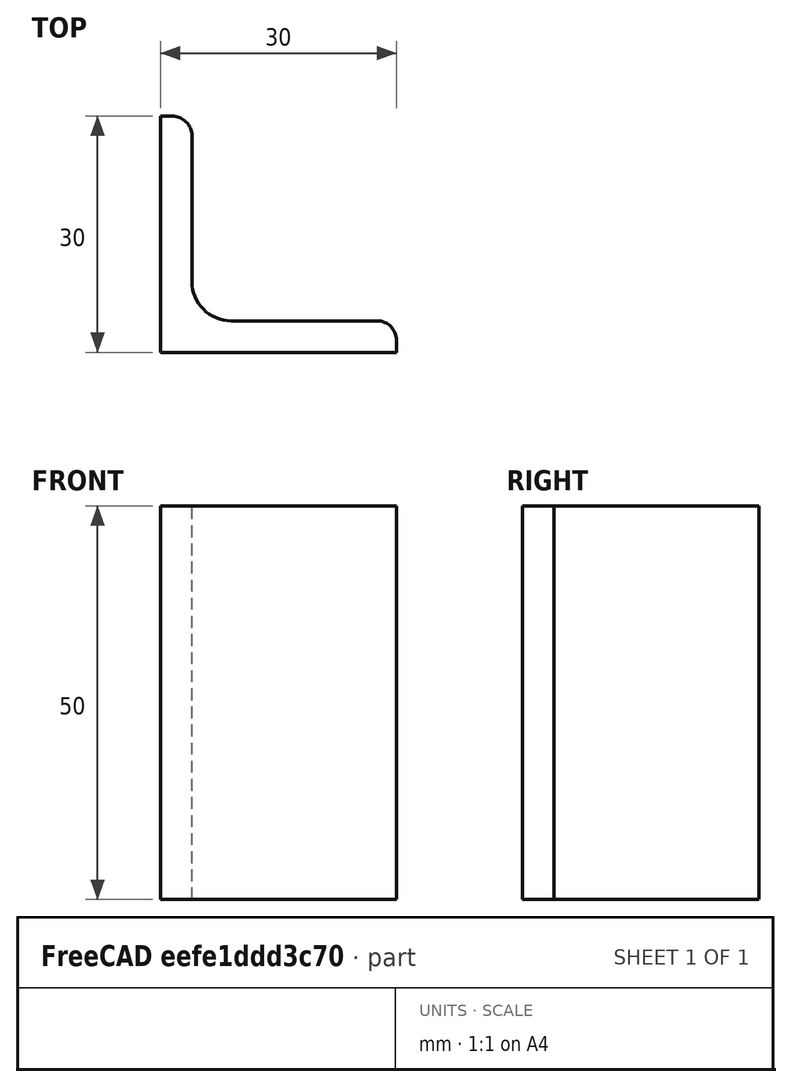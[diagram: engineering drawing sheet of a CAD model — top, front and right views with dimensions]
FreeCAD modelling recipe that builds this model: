
FCSTD DOCUMENT  (FreeCAD 0.15R4671 (Git))
Label: Angle Bar L30x30x4 EN10056 S235JR
License: All rights reserved
LicenseURL: http://en.wikipedia.org/wiki/All_rights_reserved
objects: Sketcher::SketchObject×1, Part::Extrusion×1
note: 2 computed .brp shape members not serialized (recipe doc carries the construction recipe); baked Part::Feature solids carry a one-line shape summary decoded from their .brp

FEATURE [Sketcher::SketchObject] Sketch
  sketch-geometry (9):
    g0: LineSegment StartX=0 StartY=0 StartZ=0 EndX=30 EndY=0 EndZ=0
    g1: LineSegment StartX=30 StartY=0 StartZ=0 EndX=30 EndY=1.5 EndZ=0
    g2: LineSegment StartX=27.5 StartY=4 StartZ=0 EndX=9 EndY=4 EndZ=0
    g3: LineSegment StartX=0 StartY=0 StartZ=0 EndX=0 EndY=30 EndZ=0
    g4: LineSegment StartX=0 StartY=30 StartZ=0 EndX=1.5 EndY=30 EndZ=0
    g5: LineSegment StartX=4 StartY=27.5 StartZ=0 EndX=4 EndY=9 EndZ=0
    g6: ArcOfCircle CenterX=9 CenterY=9 CenterZ=0 NormalX=0 NormalY=0 NormalZ=1 Radius=5 StartAngle=3.14159 EndAngle=4.71239
    g7: ArcOfCircle CenterX=1.5 CenterY=27.5 CenterZ=0 NormalX=0 NormalY=0 NormalZ=1 Radius=2.5 StartAngle=0 EndAngle=1.5708
    g8: ArcOfCircle CenterX=27.5 CenterY=1.5 CenterZ=0 NormalX=0 NormalY=0 NormalZ=1 Radius=2.5 StartAngle=0 EndAngle=1.5708
  constraints (23):
    c: Coincident(g0,g-1)
    c: Horizontal(g0)
    c: Coincident(g1,g0)
    c: Vertical(g1)
    c: Horizontal(g2)
    c: Coincident(g3,g-1)
    c: Vertical(g3)
    c: Coincident(g4,g3)
    c: Horizontal(g4)
    c: Vertical(g5)
    c: Tangent(g5,g6) = -1.5708
    c: Tangent(g2,g6) = 1.5708
    c: Tangent(g4,g7) = 1.5708
    c: Tangent(g5,g7) = 1.5708
    c: Tangent(g2,g8) = -1.5708
    c: Tangent(g1,g8) = -1.5708
    c: DistanceX(g0) = 30
    c: DistanceY(g3) = 30
    c: DistanceY(g0,g2) = 4
    c: DistanceX(g3,g5) = 4
    c: Radius(g6) = 5
    c: Radius(g8) = 2.5
    c: Radius(g7) = 2.5
FEATURE [Part::Extrusion] Extrude  label="Angle Bar L30x30x4 EN10056 S235JR"
  Base = -> Sketch
  Dir = (0,0,50)
  Solid = true
